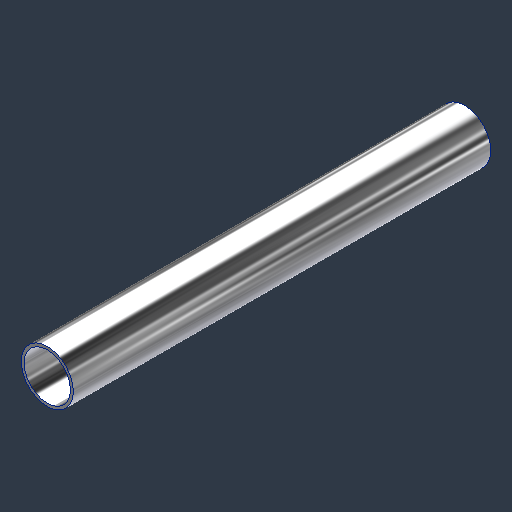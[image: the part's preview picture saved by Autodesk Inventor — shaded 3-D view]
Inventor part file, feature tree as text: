
AUTODESK INVENTOR PART (.ipt)
format: ipt  version: 2024.3 (Build 283343000, 343)  size: 134,144 bytes
history: native  units: mm (DEFAULTED — no unit token found)
features: extrude x1, sketch x1
ambient origin geometry x8: Origin, YZ Plane, XZ Plane, XY Plane, X Axis, Y Axis, Z Axis, Center Point
bodies: Solid1 (feature_tree)
feature tree (2):
  extrude  "Extrusion1"  Depth=254.0mm
  sketch  "Sketch2"  dims[d0=31.75mm d1=1.778mm d2=254.0mm d3=0.0mm]
